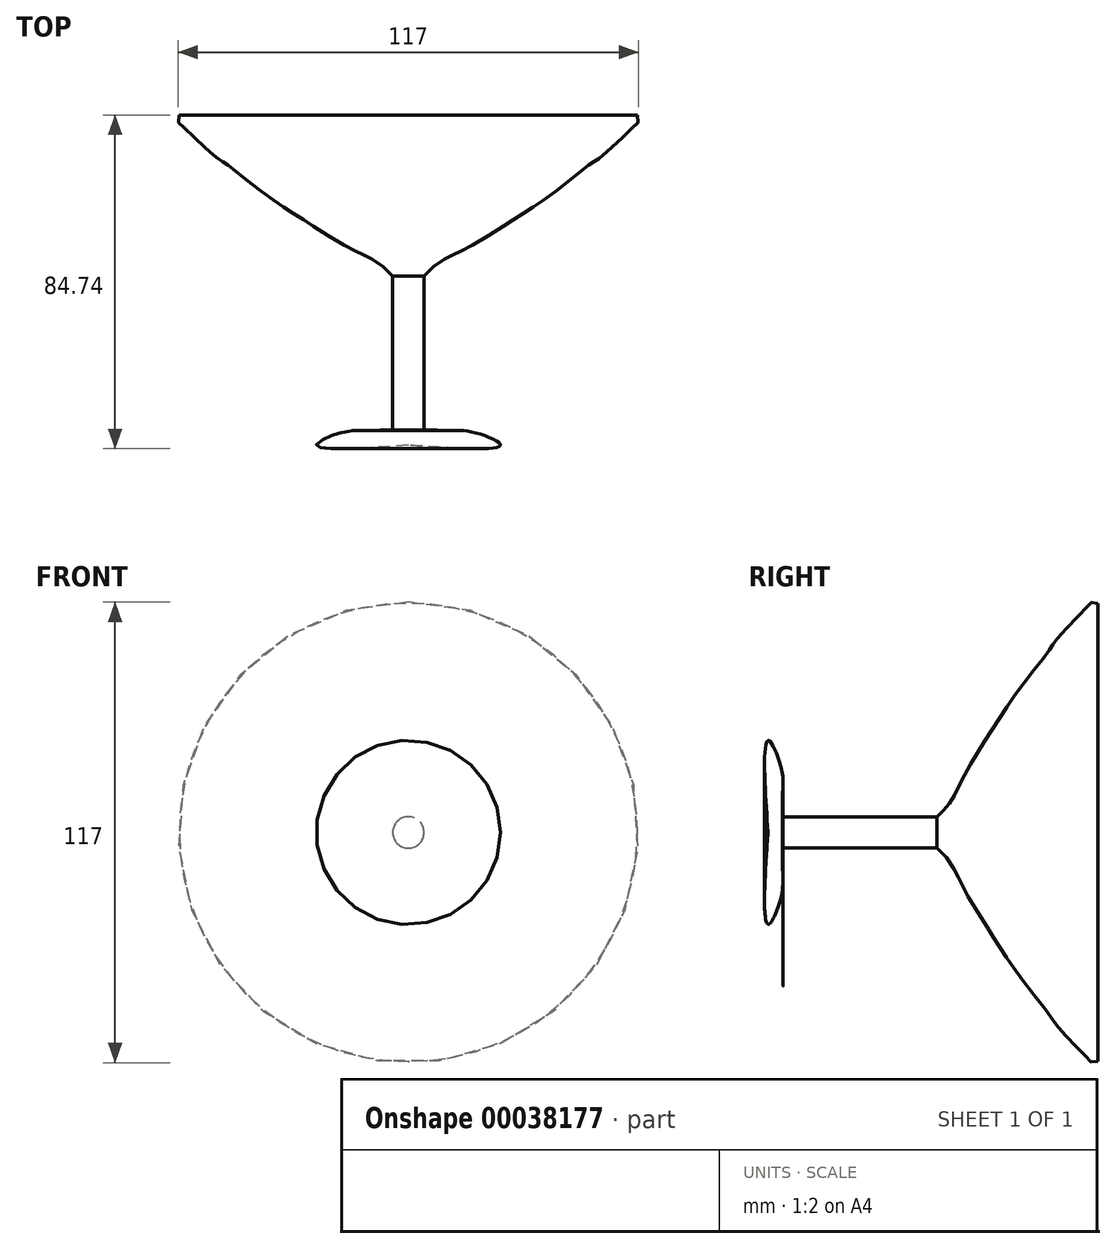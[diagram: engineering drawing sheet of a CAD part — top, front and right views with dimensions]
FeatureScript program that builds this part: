
annotation { "Feature Type Name" : "Feature", "Feature Type Description" : "" }
export const myFeature = defineFeature(function(context is Context, id is Id, definition is map)
    precondition{}
    {
        {
            var Q0;
            Q0=qCreatedBy(makeId("Top.planeOp"),FACE);
            var sketch = newSketch(context, id + "F0", { "sketchPlane" : qUnion([Q0])});
            skLineSegment(sketch, "E0", {"start": v(0, 40.93) * mm, "end": v(0, -42.93) * mm});
            skLineSegment(sketch, "E1", {"start": v(0, 40.93) * mm, "end": v(58.19, 40.93) * mm});
            skFitSpline(sketch, "E2", {"points": [v(58.19, 40.93) * mm, v(58.19, 38.94) * mm, v(49.35, 30.66) * mm, v(46.5, 28.67) * mm, v(36.51, 20.97) * mm, v(25.39, 13.55) * mm, v(15.12, 7.27) * mm, v(7.99, 3.57) * mm, v(4, 0) * mm], "startDerivative": vector(15.33, -86.17) * mm, "endDerivative": vector(-37.38, -41.8) * mm});
            skLineSegment(sketch, "E3", {"start": v(4, 0) * mm, "end": v(4, -39.22) * mm});
            skFitSpline(sketch, "E4", {"points": [v(4, -39.22) * mm, v(9.98, -39.22) * mm, v(15.97, -39.5) * mm, v(23.39, -42.93) * mm, v(0, -42.93) * mm], "startDerivative": vector(31.03, 3.77) * mm, "endDerivative": vector(-69.82, 5.2) * mm});
            skSolve(sketch);
        }
        {
            var Q0;
            Q0=makeQuery(id+"F0.imprint","IMPRINT",FACE,{"disambiguationData":[TD([[makeQuery(id+"F0.imprint","IMPRINT",EDGE,{"derivedFrom":sQuery(id+"F0.wireOp",EDGE,"E0")}),1.0]])]});
            var Q1;
            Q1=sQuery(id+"F0.wireOp",EDGE,"E0");
            revolve(context, id + "F1", {"entities" : qUnion([Q0]), "axis" : qUnion([Q1]), "revolveType" : RevolveType.FULL});
        }
    });
